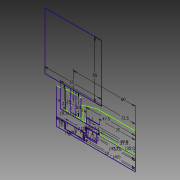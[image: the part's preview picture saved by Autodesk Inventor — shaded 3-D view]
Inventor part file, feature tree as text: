
AUTODESK INVENTOR PART (.ipt)
format: ipt  version: 2020 (Build 240168000, 168)  size: 130,048 bytes
history: native  units: mm
features: sketch x1
ambient origin geometry x8: Origin, YZ Plane, XZ Plane, XY Plane, X Axis, Y Axis, Z Axis, Center Point
feature tree (1):
  sketch  "Sketch1"  dims[d4=47.5mm d5=35.0mm d6=5.0mm d7=7.0mm d8=37.5mm d9=47.5mm d12=50.0mm d13=67.5mm d14=6.0mm d17=4.0mm d19=55.0mm d20=55.0mm d21=20.0mm d22=5.0mm d23=72.5mm d24=60.0mm d25=22.0mm d26=15.0mm d27=1.0mm d29=0.2mm d30=2.0mm d31=0.2mm d32=1.0mm d33=1.0mm d35=0.2mm d36=0.2mm d37=0.2mm d38=1.0mm d39=1.0mm d40=0.5mm d41=0.5mm d42=3.0mm d43=0.2mm d44=0.2mm d45=3.0mm d46=1.0mm d47=0.2mm d48=35.0mm d49=47.7mm d50=7.2mm d51=8.2mm d52=1.3mm d53=8.0mm d54=5.4mm d55=19.5mm d56=49.0mm]
